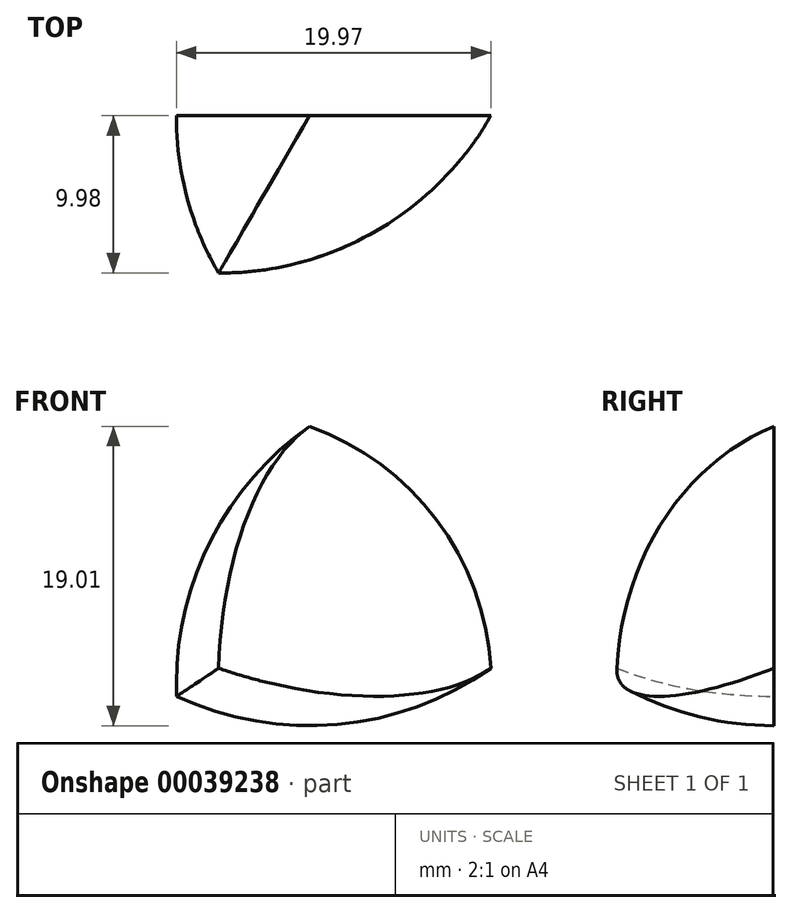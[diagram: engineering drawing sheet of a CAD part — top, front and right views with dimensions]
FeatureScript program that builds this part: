
annotation { "Feature Type Name" : "Feature", "Feature Type Description" : "" }
export const myFeature = defineFeature(function(context is Context, id is Id, definition is map)
    precondition{}
    {
        {
            var Q0;
            Q0=qCreatedBy(makeId("Top.planeOp"),FACE);
            var sketch = newSketch(context, id + "F0", { "sketchPlane" : qUnion([Q0])});
            skCircle(sketch, "E0", {"center": v(11.55, 0) * mm, "radius": 20 * mm});
            skCircle(sketch, "E1.1.0", {"center": v(-5.77, 10) * mm, "radius": 20 * mm});
            skCircle(sketch, "E1.2.0", {"center": v(-5.77, -10) * mm, "radius": 20 * mm});
            skPoint(sketch, "E1.center", {"position": v(0, 0) * mm});
            skLineSegment(sketch, "E2", {"start": v(31.55, 0) * mm, "end": v(-8.45, 0) * mm});
            skLineSegment(sketch, "E3", {"start": v(0, 0) * mm, "end": v(-5.77, -10) * mm});
            skLineSegment(sketch, "E4", {"start": v(-5.77, -10) * mm, "end": v(-15.77, -27.32) * mm});
            skLineSegment(sketch, "E5", {"start": v(0, 0) * mm, "end": v(4.23, 7.32) * mm});
            skLineSegment(sketch, "E6", {"start": v(-5.77, 10) * mm, "end": v(0, 0) * mm});
            skLineSegment(sketch, "E7", {"start": v(0, 0) * mm, "end": v(4.23, -7.32) * mm});
            skLineSegment(sketch, "E8", {"start": v(-5.77, 10) * mm, "end": v(-15.77, 27.32) * mm});
            skSolve(sketch);
        }
        {
            var Q0;
            {var subQ1=sQuery(id+"F0.wireOp",EDGE,"E2");var subQ3=sQuery(id+"F0.wireOp",EDGE,"E0");var subQ5=makeQuery(id+"F0.imprint","INTERSECT",VERTEX,{"disambiguationData":[OD(0.0)],"derivedFrom":[subQ3,subQ1]});Q0=makeQuery(id+"F0.imprint","IMPRINT",FACE,{"disambiguationData":[TD([[makeQuery(id+"F0.imprint","IMPRINT",EDGE,{"disambiguationData":[TD([[subQ5,-1.0]])],"derivedFrom":subQ3}),1.0]])]});}
            var Q1;
            {var subQ1=sQuery(id+"F0.wireOp",EDGE,"E0");var subQ4=sQuery(id+"F0.wireOp",EDGE,"E1.1.0");var subQ6=makeQuery(id+"F0.imprint","INTERSECT",VERTEX,{"derivedFrom":[subQ1,subQ4]});Q1=makeQuery(id+"F0.imprint","IMPRINT",FACE,{"disambiguationData":[TD([[makeQuery(id+"F0.imprint","IMPRINT",EDGE,{"disambiguationData":[TD([[subQ6,1.0]])],"derivedFrom":subQ4}),1.0]])]});}
            var Q2;
            {var subQ1=sQuery(id+"F0.wireOp",EDGE,"E5");Q2=makeQuery(id+"F0.imprint","IMPRINT",FACE,{"disambiguationData":[TD([[makeQuery(id+"F0.imprint","IMPRINT",EDGE,{"derivedFrom":subQ1}),1.0]])]});}
            var Q3;
            {var subQ0=sQuery(id+"F0.wireOp",EDGE,"E5");Q3=makeQuery(id+"F0.imprint","IMPRINT",FACE,{"disambiguationData":[TD([[makeQuery(id+"F0.imprint","IMPRINT",EDGE,{"derivedFrom":subQ0}),-1.0]])]});}
            var Q4;
            {var subQ0=sQuery(id+"F0.wireOp",EDGE,"E6");Q4=makeQuery(id+"F0.imprint","IMPRINT",FACE,{"disambiguationData":[TD([[makeQuery(id+"F0.imprint","IMPRINT",EDGE,{"derivedFrom":subQ0}),-1.0]])]});}
            var Q5;
            Q5=sQuery(id+"F0.wireOp",EDGE,"E2");
            revolve(context, id + "F1", {"entities" : qUnion([Q0, Q1, Q2, Q3, Q4]), "axis" : qUnion([Q5]), "revolveType" : RevolveType.FULL});
        }
        {
            var Q0;
            {var subQ1=sQuery(id+"F0.wireOp",EDGE,"E0");var subQ4=sQuery(id+"F0.wireOp",EDGE,"E1.1.0");var subQ6=makeQuery(id+"F0.imprint","INTERSECT",VERTEX,{"derivedFrom":[subQ1,subQ4]});Q0=makeQuery(id+"F0.imprint","IMPRINT",FACE,{"disambiguationData":[TD([[makeQuery(id+"F0.imprint","IMPRINT",EDGE,{"disambiguationData":[TD([[subQ6,1.0]])],"derivedFrom":subQ4}),1.0]])]});}
            var Q1;
            {var subQ0=sQuery(id+"F0.wireOp",EDGE,"E5");Q1=makeQuery(id+"F0.imprint","IMPRINT",FACE,{"disambiguationData":[TD([[makeQuery(id+"F0.imprint","IMPRINT",EDGE,{"derivedFrom":subQ0}),-1.0]])]});}
            var Q2;
            {var subQ1=sQuery(id+"F0.wireOp",EDGE,"E5");Q2=makeQuery(id+"F0.imprint","IMPRINT",FACE,{"disambiguationData":[TD([[makeQuery(id+"F0.imprint","IMPRINT",EDGE,{"derivedFrom":subQ1}),1.0]])]});}
            var Q3;
            {var subQ3=sQuery(id+"F0.wireOp",EDGE,"E7");Q3=makeQuery(id+"F0.imprint","IMPRINT",FACE,{"disambiguationData":[TD([[makeQuery(id+"F0.imprint","IMPRINT",EDGE,{"derivedFrom":subQ3}),1.0]])]});}
            var Q4;
            {var subQ0=sQuery(id+"F0.wireOp",EDGE,"E8");Q4=makeQuery(id+"F0.imprint","IMPRINT",FACE,{"disambiguationData":[TD([[makeQuery(id+"F0.imprint","IMPRINT",EDGE,{"derivedFrom":subQ0}),-1.0]])]});}
            var Q5;
            Q5=sQuery(id+"F0.wireOp",EDGE,"E8");
            revolve(context, id + "F2", {"entities" : qUnion([Q0, Q1, Q2, Q3, Q4]), "axis" : qUnion([Q5]), "revolveType" : RevolveType.FULL});
        }
        {
            var Q0;
            {var subQ3=sQuery(id+"F0.wireOp",EDGE,"E4");Q0=makeQuery(id+"F0.imprint","IMPRINT",FACE,{"disambiguationData":[TD([[makeQuery(id+"F0.imprint","IMPRINT",EDGE,{"derivedFrom":subQ3}),-1.0]])]});}
            var Q1;
            {var subQ3=sQuery(id+"F0.wireOp",EDGE,"E0");var subQ6=makeQuery(id+"F0.imprint","INTERSECT",VERTEX,{"disambiguationData":[OD(1.0)],"derivedFrom":[subQ3,sQuery(id+"F0.wireOp",EDGE,"E2")]});Q1=makeQuery(id+"F0.imprint","IMPRINT",FACE,{"disambiguationData":[TD([[makeQuery(id+"F0.imprint","IMPRINT",EDGE,{"disambiguationData":[TD([[subQ6,1.0]])],"derivedFrom":subQ3}),-1.0]])]});}
            var Q2;
            {var subQ0=sQuery(id+"F0.wireOp",EDGE,"E3");Q2=makeQuery(id+"F0.imprint","IMPRINT",FACE,{"disambiguationData":[TD([[makeQuery(id+"F0.imprint","IMPRINT",EDGE,{"derivedFrom":subQ0}),-1.0]])]});}
            var Q3;
            {var subQ0=sQuery(id+"F0.wireOp",EDGE,"E6");Q3=makeQuery(id+"F0.imprint","IMPRINT",FACE,{"disambiguationData":[TD([[makeQuery(id+"F0.imprint","IMPRINT",EDGE,{"derivedFrom":subQ0}),-1.0]])]});}
            var Q4;
            {var subQ1=sQuery(id+"F0.wireOp",EDGE,"E5");Q4=makeQuery(id+"F0.imprint","IMPRINT",FACE,{"disambiguationData":[TD([[makeQuery(id+"F0.imprint","IMPRINT",EDGE,{"derivedFrom":subQ1}),1.0]])]});}
            var Q5;
            Q5=sQuery(id+"F0.wireOp",EDGE,"E4");
            revolve(context, id + "F3", {"entities" : qUnion([Q0, Q1, Q2, Q3, Q4]), "axis" : qUnion([Q5]), "revolveType" : RevolveType.FULL});
        }
        {
            var Q0;
            Q0=qCreatedBy(makeId("Top.planeOp"),FACE);
            cPlane(context, id + "F4", {"entities" : qUnion([Q0]), "cplaneType" : CPlaneType.OFFSET, "offset" : 17.32 * mm, "width" : 150 * mm, "height" : 150 * mm});
        }
        {
            var Q0;
            Q0=qCreatedBy(id+"F4.planeOp",FACE);
            var sketch = newSketch(context, id + "F5", { "sketchPlane" : qUnion([Q0])});
            skCircle(sketch, "E9", {"center": v(0, 0) * mm, "radius": 20 * mm});
            skLineSegment(sketch, "E10", {"start": v(20, 0) * mm, "end": v(-20, 0) * mm});
            skSolve(sketch);
        }
        {
            var Q0;
            {var subQ0=sQuery(id+"F5.wireOp",EDGE,"E10");Q0=makeQuery(id+"F5.imprint","IMPRINT",FACE,{"disambiguationData":[TD([[makeQuery(id+"F5.imprint","IMPRINT",EDGE,{"derivedFrom":subQ0}),-1.0]])]});}
            var Q1;
            Q1=sQuery(id+"F5.wireOp",EDGE,"E10");
            revolve(context, id + "F6", {"entities" : qUnion([Q0]), "axis" : qUnion([Q1]), "revolveType" : RevolveType.FULL});
        }
        {
            var Q0;
            Q0=makeQuery(id+"F6.opRevolve","SWEPT_BODY",BODY,{"disambiguationData":[OSD([sQuery(id+"F5.wireOp",EDGE,"E9"),sQuery(id+"F5.wireOp",EDGE,"E10")])]});
            var Q1;
            Q1=makeQuery(id+"F1.opRevolve","SWEPT_BODY",BODY,{"disambiguationData":[OSD([sQuery(id+"F0.wireOp",EDGE,"E0"),sQuery(id+"F0.wireOp",EDGE,"E2")])]});
            var Q2;
            Q2=makeQuery(id+"F3.opRevolve","SWEPT_BODY",BODY,{"disambiguationData":[OSD([sQuery(id+"F0.wireOp",EDGE,"E1.2.0"),sQuery(id+"F0.wireOp",EDGE,"E3"),sQuery(id+"F0.wireOp",EDGE,"E4"),sQuery(id+"F0.wireOp",EDGE,"E5")])]});
            var Q3;
            Q3=makeQuery(id+"F2.opRevolve","SWEPT_BODY",BODY,{"disambiguationData":[OSD([sQuery(id+"F0.wireOp",EDGE,"E1.1.0"),sQuery(id+"F0.wireOp",EDGE,"E6"),sQuery(id+"F0.wireOp",EDGE,"E7"),sQuery(id+"F0.wireOp",EDGE,"E8")])]});
            booleanBodies(context, id + "F7", {"operationType" : BooleanOperationType.INTERSECTION, "tools" : qUnion([Q0, Q1, Q2, Q3])});
        }
        {
            var Q0;
            Q0=qCreatedBy(makeId("Front.planeOp"),FACE);
            var sketch = newSketch(context, id + "F8", { "sketchPlane" : qUnion([Q0])});
            skLineSegment(sketch, "E11.bottom", {"start": v(-24.13, 26.48) * mm, "end": v(23.54, 26.48) * mm});
            skLineSegment(sketch, "E11.top", {"start": v(-24.13, -12.28) * mm, "end": v(23.54, -12.28) * mm});
            skLineSegment(sketch, "E11.left", {"start": v(-24.13, 26.48) * mm, "end": v(-24.13, -12.28) * mm});
            skLineSegment(sketch, "E11.right", {"start": v(23.54, 26.48) * mm, "end": v(23.54, -12.28) * mm});
            skSolve(sketch);
        }
        {
            var Q0;
            Q0=qSketchRegion(id+"F8",true);
            extrude(context, id + "F9", {"entities" : qUnion([Q0]), "oppositeDirection" : true, "depth" : 25 * mm});
        }
        {
            var Q0;
            Q0=makeQuery(id+"F9.opExtrude","SWEPT_BODY",BODY,{"disambiguationData":[OSD([sQuery(id+"F8.wireOp",EDGE,"E11.bottom"),sQuery(id+"F8.wireOp",EDGE,"E11.top"),sQuery(id+"F8.wireOp",EDGE,"E11.left"),sQuery(id+"F8.wireOp",EDGE,"E11.right")])]});
            var Q1;
            Q1=makeQuery(id+"F7.opBoolean","INTERSECT",BODY,{"derivedFrom":[makeQuery(id+"F1.opRevolve","SWEPT_BODY",BODY,{"disambiguationData":[OSD([sQuery(id+"F0.wireOp",EDGE,"E0"),sQuery(id+"F0.wireOp",EDGE,"E2")])]}),makeQuery(id+"F2.opRevolve","SWEPT_BODY",BODY,{"disambiguationData":[OSD([sQuery(id+"F0.wireOp",EDGE,"E1.1.0"),sQuery(id+"F0.wireOp",EDGE,"E6"),sQuery(id+"F0.wireOp",EDGE,"E7"),sQuery(id+"F0.wireOp",EDGE,"E8")])]}),makeQuery(id+"F3.opRevolve","SWEPT_BODY",BODY,{"disambiguationData":[OSD([sQuery(id+"F0.wireOp",EDGE,"E1.2.0"),sQuery(id+"F0.wireOp",EDGE,"E3"),sQuery(id+"F0.wireOp",EDGE,"E4"),sQuery(id+"F0.wireOp",EDGE,"E5")])]}),makeQuery(id+"F6.opRevolve","SWEPT_BODY",BODY,{"disambiguationData":[OSD([sQuery(id+"F5.wireOp",EDGE,"E9"),sQuery(id+"F5.wireOp",EDGE,"E10")])]})]});
            booleanBodies(context, id + "F10", {"operationType" : BooleanOperationType.SUBTRACTION, "tools" : qUnion([Q0]), "targets" : qUnion([Q1])});
        }
    });
